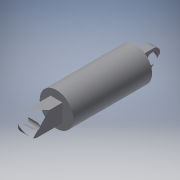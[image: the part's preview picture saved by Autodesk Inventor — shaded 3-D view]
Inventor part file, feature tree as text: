
AUTODESK INVENTOR PART (.ipt)
format: ipt  version: 2016 (Build 200138000, 138)  size: 142,336 bytes
history: native  units: mm
features: extrude x5, sketch x3, fillet x2
ambient origin geometry x8: Origin, YZ Plane, XZ Plane, XY Plane, X Axis, Y Axis, Z Axis, Center Point
bodies: Solid1 (feature_tree)
feature tree (10):
  extrude  "Extrusion1"  Depth=40.0mm TaperAngle=0.0deg
  extrude  "Extrusion2"  Depth=8.5mm
  fillet  "Fillet1"  Radius=8.5mm
  extrude  "Extrusion3"  Depth=10.6mm TaperAngle=0.0deg
  extrude  "Extrusion4"  Depth=3.5mm
  fillet  "Fillet2"  Radius=5.5mm
  extrude  "Extrusion5"  Depth=4.0mm TaperAngle=0.0deg
  sketch  "Sketch1"  dims[d0=17.0mm d1=40.0mm d2=0.0mm]
  sketch  "Sketch2"  dims[d3=4.25mm d4=2.0mm d5=8.5mm]
  sketch  "Sketch4"  dims[d6=4.0mm d7=10.6mm d8=0.0mm d9=3.5mm d11=5.5mm d12=10.5mm d13=0.0mm d14=4.5mm d15=3.0mm d16=9.0mm d17=6.0mm d18=16.6mm d19=0.0mm d20=4.0mm d22=3.0mm d23=16.5mm d24=0.0mm d26=4.15mm d27=3.9mm]
